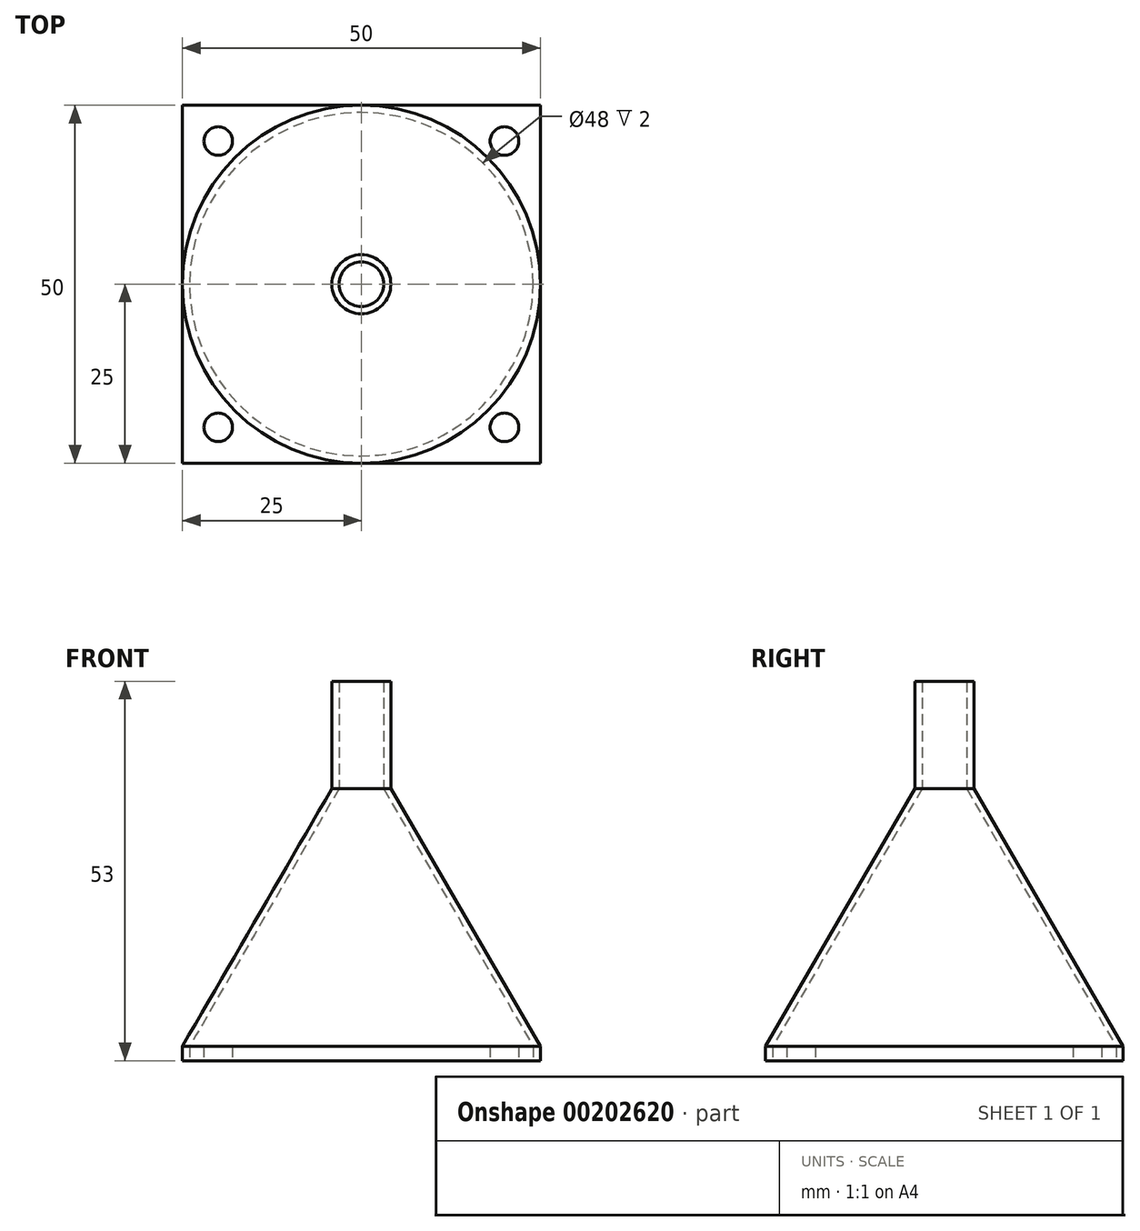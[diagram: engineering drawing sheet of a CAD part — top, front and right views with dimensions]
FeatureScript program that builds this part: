
annotation { "Feature Type Name" : "Feature", "Feature Type Description" : "" }
export const myFeature = defineFeature(function(context is Context, id is Id, definition is map)
    precondition{}
    {
        {
            var Q0;
            Q0=qCreatedBy(makeId("Top.planeOp"),FACE);
            var sketch = newSketch(context, id + "F0", { "sketchPlane" : qUnion([Q0])});
            skLineSegment(sketch, "E0.bottom", {"start": v(25, 25) * mm, "end": v(-25, 25) * mm});
            skLineSegment(sketch, "E0.top", {"start": v(25, -25) * mm, "end": v(-25, -25) * mm});
            skLineSegment(sketch, "E0.left", {"start": v(25, 25) * mm, "end": v(25, -25) * mm});
            skLineSegment(sketch, "E0.right", {"start": v(-25, 25) * mm, "end": v(-25, -25) * mm});
            skPoint(sketch, "E0.middle", {"position": v(0, 0) * mm});
            skSolve(sketch);
        }
        {
            var Q0;
            Q0=makeQuery(id+"F0.imprint","IMPRINT",FACE,{"disambiguationData":[TD([[makeQuery(id+"F0.imprint","IMPRINT",EDGE,{"derivedFrom":sQuery(id+"F0.wireOp",EDGE,"E0.bottom")}),1.0]])]});
            extrude(context, id + "F1", {"entities" : qUnion([Q0]), "depth" : 2 * mm});
        }
        {
            var Q0;
            Q0=makeQuery(id+"F1.opExtrude","CAP_FACE",FACE,{"disambiguationData":[OSD([sQuery(id+"F0.wireOp",EDGE,"E0.bottom"),sQuery(id+"F0.wireOp",EDGE,"E0.top"),sQuery(id+"F0.wireOp",EDGE,"E0.left"),sQuery(id+"F0.wireOp",EDGE,"E0.right")])],"isStart":true});
            var sketch = newSketch(context, id + "F2", { "sketchPlane" : qUnion([Q0])});
            skCircle(sketch, "E1", {"center": v(0, 0) * mm, "radius": 24 * mm});
            skSolve(sketch);
        }
        {
            var Q0;
            Q0=makeQuery(id+"F2.imprint","IMPRINT",FACE,{"disambiguationData":[TD([[makeQuery(id+"F2.imprint","IMPRINT",EDGE,{"derivedFrom":sQuery(id+"F2.wireOp",EDGE,"E1")}),1.0]])]});
            extrude(context, id + "F3", {"entities" : qUnion([Q0]), "operationType" : NewBodyOperationType.REMOVE, "oppositeDirection" : true, "depth" : 25 * mm});
        }
        {
            var Q0;
            Q0=qCreatedBy(makeId("Front.planeOp"),FACE);
            var sketch = newSketch(context, id + "F4", { "sketchPlane" : qUnion([Q0])});
            skLineSegment(sketch, "E2.bottom", {"start": v(0, 0) * mm, "end": v(24, 0) * mm, "construction": true});
            skLineSegment(sketch, "E2.top", {"start": v(0, 2) * mm, "end": v(24, 2) * mm, "construction": true});
            skLineSegment(sketch, "E2.left", {"start": v(0, 0) * mm, "end": v(0, 2) * mm, "construction": true});
            skLineSegment(sketch, "E2.right", {"start": v(24, 0) * mm, "end": v(24, 2) * mm, "construction": true});
            skLineSegment(sketch, "E3", {"start": v(0, 2) * mm, "end": v(0, 38) * mm, "construction": true});
            skLineSegment(sketch, "E4", {"start": v(0, 38) * mm, "end": v(3.12, 38) * mm, "construction": true});
            skLineSegment(sketch, "E5", {"start": v(24, 2) * mm, "end": v(3.12, 38) * mm});
            skLineSegment(sketch, "E6", {"start": v(3.12, 38) * mm, "end": v(3.12, 53) * mm});
            skLineSegment(sketch, "E7", {"start": v(3.12, 53) * mm, "end": v(4.12, 53) * mm});
            skLineSegment(sketch, "E8", {"start": v(4.12, 53) * mm, "end": v(4.12, 38) * mm});
            skLineSegment(sketch, "E9", {"start": v(4.12, 38) * mm, "end": v(25, 2) * mm});
            skLineSegment(sketch, "E10", {"start": v(25, 2) * mm, "end": v(24, 2) * mm});
            skSolve(sketch);
        }
        {
            var Q0;
            Q0=makeQuery(id+"F1.opExtrude","CAP_FACE",FACE,{"disambiguationData":[OSD([sQuery(id+"F0.wireOp",EDGE,"E0.bottom"),sQuery(id+"F0.wireOp",EDGE,"E0.top"),sQuery(id+"F0.wireOp",EDGE,"E0.left"),sQuery(id+"F0.wireOp",EDGE,"E0.right")])],"isStart":true});
            var sketch = newSketch(context, id + "F5", { "sketchPlane" : qUnion([Q0])});
            skLineSegment(sketch, "E11.bottom", {"start": v(0, 0) * mm, "end": v(20, 0) * mm, "construction": true});
            skLineSegment(sketch, "E11.top", {"start": v(0, 20) * mm, "end": v(20, 20) * mm, "construction": true});
            skLineSegment(sketch, "E11.left", {"start": v(0, 0) * mm, "end": v(0, 20) * mm, "construction": true});
            skLineSegment(sketch, "E11.right", {"start": v(20, 0) * mm, "end": v(20, 20) * mm, "construction": true});
            skLineSegment(sketch, "E12.bottom", {"start": v(20, 20) * mm, "end": v(-20, 20) * mm, "construction": true});
            skLineSegment(sketch, "E12.top", {"start": v(20, -20) * mm, "end": v(-20, -20) * mm, "construction": true});
            skLineSegment(sketch, "E12.left", {"start": v(20, 20) * mm, "end": v(20, -20) * mm, "construction": true});
            skLineSegment(sketch, "E12.right", {"start": v(-20, 20) * mm, "end": v(-20, -20) * mm, "construction": true});
            skCircle(sketch, "E13", {"center": v(-20, 20) * mm, "radius": 2 * mm});
            skCircle(sketch, "E14", {"center": v(20, 20) * mm, "radius": 2 * mm});
            skCircle(sketch, "E15", {"center": v(20, -20) * mm, "radius": 2 * mm});
            skCircle(sketch, "E16", {"center": v(-20, -20) * mm, "radius": 2 * mm});
            skSolve(sketch);
        }
        {
            var Q0;
            Q0 = qSketchRegion(id + "F5", true);
            extrude(context, id + "F6", {"entities" : qUnion([Q0]), "operationType" : NewBodyOperationType.REMOVE, "endBound" : BoundingType.THROUGH_ALL, "oppositeDirection" : true, "depth" : 25 * mm});
        }
        {
            var Q0;
            Q0 = qSketchRegion(id + "F4", true);
            var Q1;
            Q1=sQuery(id+"F4.wireOp",EDGE,"E3");
            revolve(context, id + "F7", {"operationType" : NewBodyOperationType.ADD, "entities" : qUnion([Q0]), "axis" : qUnion([Q1]), "revolveType" : RevolveType.FULL});
        }
    });
